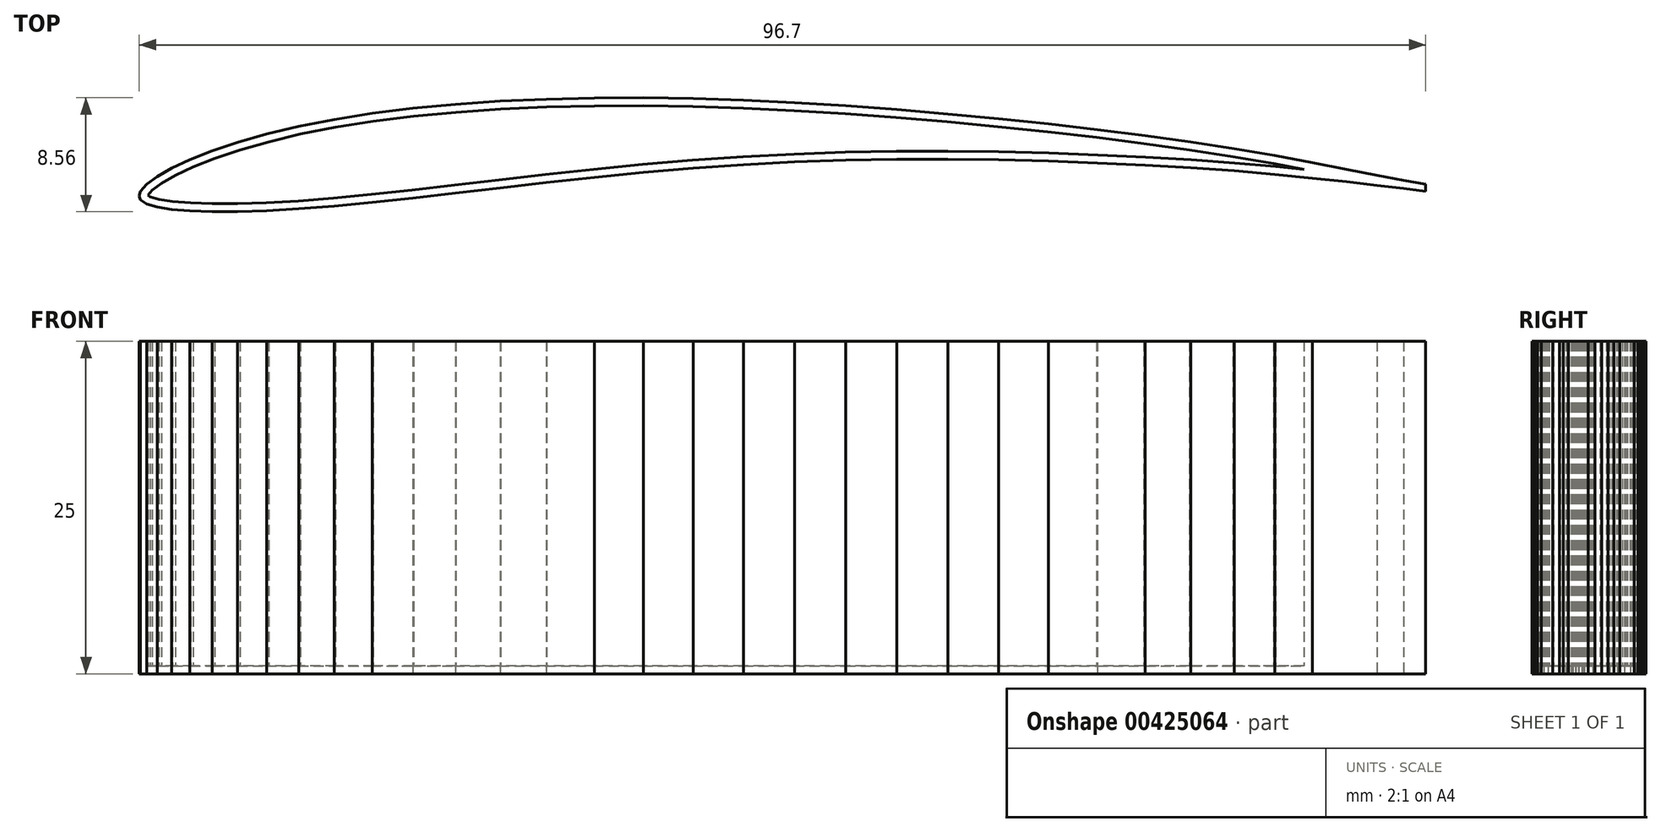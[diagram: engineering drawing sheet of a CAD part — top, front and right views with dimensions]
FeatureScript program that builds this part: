
annotation { "Feature Type Name" : "Feature", "Feature Type Description" : "" }
export const myFeature = defineFeature(function(context is Context, id is Id, definition is map)
    precondition{}
    {
        {
            var Q0;
            Q0=qCreatedBy(makeId("Top.planeOp"),FACE);
            var sketch = newSketch(context, id + "F0", { "sketchPlane" : qUnion([Q0])});
            skLineSegment(sketch, "E0", {"start": v(46.7, -2.2) * mm, "end": v(45.04, -1.92) * mm});
            skLineSegment(sketch, "E1", {"start": v(45.04, -1.92) * mm, "end": v(43.06, -1.56) * mm});
            skLineSegment(sketch, "E2", {"start": v(43.06, -1.56) * mm, "end": v(40.78, -1.1) * mm});
            skLineSegment(sketch, "E3", {"start": v(40.78, -1.1) * mm, "end": v(38.2, -0.6) * mm});
            skLineSegment(sketch, "E4", {"start": v(38.2, -0.6) * mm, "end": v(35.37, -0.07) * mm});
            skLineSegment(sketch, "E5", {"start": v(35.37, -0.07) * mm, "end": v(32.3, 0.45) * mm});
            skLineSegment(sketch, "E6", {"start": v(32.3, 0.45) * mm, "end": v(29.05, 0.96) * mm});
            skLineSegment(sketch, "E7", {"start": v(29.05, 0.96) * mm, "end": v(25.62, 1.44) * mm});
            skLineSegment(sketch, "E8", {"start": v(25.62, 1.44) * mm, "end": v(22.04, 1.9) * mm});
            skLineSegment(sketch, "E9", {"start": v(22.04, 1.9) * mm, "end": v(18.36, 2.31) * mm});
            skLineSegment(sketch, "E10", {"start": v(18.36, 2.31) * mm, "end": v(14.6, 2.7) * mm});
            skLineSegment(sketch, "E11", {"start": v(14.6, 2.7) * mm, "end": v(10.78, 3.07) * mm});
            skLineSegment(sketch, "E12", {"start": v(10.78, 3.07) * mm, "end": v(6.94, 3.4) * mm});
            skLineSegment(sketch, "E13", {"start": v(6.94, 3.4) * mm, "end": v(3.1, 3.68) * mm});
            skLineSegment(sketch, "E14", {"start": v(3.1, 3.68) * mm, "end": v(-0.73, 3.92) * mm});
            skLineSegment(sketch, "E15", {"start": v(-0.73, 3.92) * mm, "end": v(-4.56, 4.1) * mm});
            skLineSegment(sketch, "E16", {"start": v(-4.56, 4.1) * mm, "end": v(-8.36, 4.22) * mm});
            skLineSegment(sketch, "E17", {"start": v(-8.36, 4.22) * mm, "end": v(-12.11, 4.28) * mm});
            skLineSegment(sketch, "E18", {"start": v(-12.11, 4.28) * mm, "end": v(-15.8, 4.27) * mm});
            skLineSegment(sketch, "E19", {"start": v(-15.8, 4.27) * mm, "end": v(-19.4, 4.18) * mm});
            skLineSegment(sketch, "E20", {"start": v(-19.4, 4.18) * mm, "end": v(-22.88, 4.03) * mm});
            skLineSegment(sketch, "E21", {"start": v(-22.88, 4.03) * mm, "end": v(-26.24, 3.8) * mm});
            skLineSegment(sketch, "E22", {"start": v(-26.24, 3.8) * mm, "end": v(-29.45, 3.5) * mm});
            skLineSegment(sketch, "E23", {"start": v(-29.45, 3.5) * mm, "end": v(-32.5, 3.11) * mm});
            skLineSegment(sketch, "E24", {"start": v(-32.5, 3.11) * mm, "end": v(-35.35, 2.66) * mm});
            skLineSegment(sketch, "E25", {"start": v(-35.35, 2.66) * mm, "end": v(-38, 2.14) * mm});
            skLineSegment(sketch, "E26", {"start": v(-38, 2.14) * mm, "end": v(-40.42, 1.56) * mm});
            skLineSegment(sketch, "E27", {"start": v(-40.42, 1.56) * mm, "end": v(-42.6, 0.93) * mm});
            skLineSegment(sketch, "E28", {"start": v(-42.6, 0.93) * mm, "end": v(-44.53, 0.28) * mm});
            skLineSegment(sketch, "E29", {"start": v(-44.53, 0.28) * mm, "end": v(-46.19, -0.37) * mm});
            skLineSegment(sketch, "E30", {"start": v(-46.19, -0.37) * mm, "end": v(-47.57, -1.02) * mm});
            skLineSegment(sketch, "E31", {"start": v(-47.57, -1.02) * mm, "end": v(-48.66, -1.64) * mm});
            skLineSegment(sketch, "E32", {"start": v(-48.66, -1.64) * mm, "end": v(-49.45, -2.22) * mm});
            skLineSegment(sketch, "E33", {"start": v(-49.45, -2.22) * mm, "end": v(-49.9, -2.75) * mm});
            skLineSegment(sketch, "E34", {"start": v(-49.9, -2.75) * mm, "end": v(-50, -3.1) * mm});
            skLineSegment(sketch, "E35", {"start": v(-50, -3.1) * mm, "end": v(-49.9, -3.38) * mm});
            skLineSegment(sketch, "E36", {"start": v(-49.9, -3.38) * mm, "end": v(-49.45, -3.7) * mm});
            skLineSegment(sketch, "E37", {"start": v(-49.45, -3.7) * mm, "end": v(-48.66, -3.94) * mm});
            skLineSegment(sketch, "E38", {"start": v(-48.66, -3.94) * mm, "end": v(-47.57, -4.1) * mm});
            skLineSegment(sketch, "E39", {"start": v(-47.57, -4.1) * mm, "end": v(-46.19, -4.22) * mm});
            skLineSegment(sketch, "E40", {"start": v(-46.19, -4.22) * mm, "end": v(-44.53, -4.28) * mm});
            skLineSegment(sketch, "E41", {"start": v(-44.53, -4.28) * mm, "end": v(-42.6, -4.28) * mm});
            skLineSegment(sketch, "E42", {"start": v(-42.6, -4.28) * mm, "end": v(-40.42, -4.2) * mm});
            skLineSegment(sketch, "E43", {"start": v(-40.42, -4.2) * mm, "end": v(-38, -4.07) * mm});
            skLineSegment(sketch, "E44", {"start": v(-38, -4.07) * mm, "end": v(-35.35, -3.86) * mm});
            skLineSegment(sketch, "E45", {"start": v(-35.35, -3.86) * mm, "end": v(-32.5, -3.58) * mm});
            skLineSegment(sketch, "E46", {"start": v(-32.5, -3.58) * mm, "end": v(-29.45, -3.25) * mm});
            skLineSegment(sketch, "E47", {"start": v(-29.45, -3.25) * mm, "end": v(-26.24, -2.88) * mm});
            skLineSegment(sketch, "E48", {"start": v(-26.24, -2.88) * mm, "end": v(-22.88, -2.49) * mm});
            skLineSegment(sketch, "E49", {"start": v(-22.88, -2.49) * mm, "end": v(-19.4, -2.08) * mm});
            skLineSegment(sketch, "E50", {"start": v(-19.4, -2.08) * mm, "end": v(-15.8, -1.7) * mm});
            skLineSegment(sketch, "E51", {"start": v(-15.8, -1.7) * mm, "end": v(-12.11, -1.33) * mm});
            skLineSegment(sketch, "E52", {"start": v(-12.11, -1.33) * mm, "end": v(-8.36, -1.01) * mm});
            skLineSegment(sketch, "E53", {"start": v(-8.36, -1.01) * mm, "end": v(-4.56, -0.75) * mm});
            skLineSegment(sketch, "E54", {"start": v(-4.56, -0.75) * mm, "end": v(-0.74, -0.55) * mm});
            skLineSegment(sketch, "E55", {"start": v(-0.73, -0.55) * mm, "end": v(3.1, -0.41) * mm});
            skLineSegment(sketch, "E56", {"start": v(3.1, -0.41) * mm, "end": v(6.94, -0.34) * mm});
            skLineSegment(sketch, "E57", {"start": v(6.94, -0.34) * mm, "end": v(10.78, -0.33) * mm});
            skLineSegment(sketch, "E58", {"start": v(10.78, -0.33) * mm, "end": v(14.6, -0.38) * mm});
            skLineSegment(sketch, "E59", {"start": v(14.6, -0.38) * mm, "end": v(18.36, -0.48) * mm});
            skLineSegment(sketch, "E60", {"start": v(18.36, -0.48) * mm, "end": v(22.04, -0.62) * mm});
            skLineSegment(sketch, "E61", {"start": v(22.04, -0.62) * mm, "end": v(25.62, -0.78) * mm});
            skLineSegment(sketch, "E62", {"start": v(25.62, -0.78) * mm, "end": v(29.05, -0.98) * mm});
            skLineSegment(sketch, "E63", {"start": v(29.05, -0.98) * mm, "end": v(32.3, -1.21) * mm});
            skLineSegment(sketch, "E64", {"start": v(32.3, -1.21) * mm, "end": v(35.37, -1.47) * mm});
            skLineSegment(sketch, "E65", {"start": v(35.37, -1.47) * mm, "end": v(38.2, -1.75) * mm});
            skLineSegment(sketch, "E66", {"start": v(38.2, -1.75) * mm, "end": v(40.78, -2.04) * mm});
            skLineSegment(sketch, "E67", {"start": v(40.78, -2.04) * mm, "end": v(43.06, -2.3) * mm});
            skLineSegment(sketch, "E68", {"start": v(43.06, -2.3) * mm, "end": v(45.04, -2.54) * mm});
            skLineSegment(sketch, "E69", {"start": v(45.04, -2.54) * mm, "end": v(46.7, -2.74) * mm});
            skLineSegment(sketch, "E70", {"start": v(-50, -3.07) * mm, "end": v(50, -3.07) * mm, "construction": true});
            skLineSegment(sketch, "E71", {"start": v(46.7, -2.2) * mm, "end": v(46.7, -2.74) * mm});
            skLineSegment(sketch, "E72", {"start": v(35.37, -0.07) * mm, "end": v(35.37, -1.47) * mm});
            skSolve(sketch);
        }
        {
            var Q0;
            Q0 = qSketchRegion(id + "F0", true);
            extrude(context, id + "F1", {"entities" : qUnion([Q0]), "depth" : 25 * mm});
        }
        {
            var Q0;
            Q0=makeQuery(id+"F1.opExtrude","CAP_FACE",FACE,{"disambiguationData":[OSD([sQuery(id+"F0.wireOp",EDGE,"727b936a-63c7-4c52-894b-6a5cdd6f010b"),sQuery(id+"F0.wireOp",EDGE,"iox4s91j-Nup9-9dsc-COxM-rL3S8vBAQRYW")])],"isStart":false});
            var Q1;
            Q1=makeQuery(id+"F1.opExtrude","CAP_FACE",FACE,{"disambiguationData":[OSD([sQuery(id+"F0.wireOp",EDGE,"E0"),sQuery(id+"F0.wireOp",EDGE,"E1"),sQuery(id+"F0.wireOp",EDGE,"E2"),sQuery(id+"F0.wireOp",EDGE,"E3"),sQuery(id+"F0.wireOp",EDGE,"E4"),sQuery(id+"F0.wireOp",EDGE,"E5"),sQuery(id+"F0.wireOp",EDGE,"E6"),sQuery(id+"F0.wireOp",EDGE,"E7"),sQuery(id+"F0.wireOp",EDGE,"E8"),sQuery(id+"F0.wireOp",EDGE,"E9"),sQuery(id+"F0.wireOp",EDGE,"E10"),sQuery(id+"F0.wireOp",EDGE,"E11"),sQuery(id+"F0.wireOp",EDGE,"E12"),sQuery(id+"F0.wireOp",EDGE,"E13"),sQuery(id+"F0.wireOp",EDGE,"E14"),sQuery(id+"F0.wireOp",EDGE,"E15"),sQuery(id+"F0.wireOp",EDGE,"E16"),sQuery(id+"F0.wireOp",EDGE,"E17"),sQuery(id+"F0.wireOp",EDGE,"E18"),sQuery(id+"F0.wireOp",EDGE,"E19"),sQuery(id+"F0.wireOp",EDGE,"E20"),sQuery(id+"F0.wireOp",EDGE,"E21"),sQuery(id+"F0.wireOp",EDGE,"E22"),sQuery(id+"F0.wireOp",EDGE,"E23"),sQuery(id+"F0.wireOp",EDGE,"E24"),sQuery(id+"F0.wireOp",EDGE,"E25"),sQuery(id+"F0.wireOp",EDGE,"E26"),sQuery(id+"F0.wireOp",EDGE,"E27"),sQuery(id+"F0.wireOp",EDGE,"E28"),sQuery(id+"F0.wireOp",EDGE,"E29"),sQuery(id+"F0.wireOp",EDGE,"E30"),sQuery(id+"F0.wireOp",EDGE,"E31"),sQuery(id+"F0.wireOp",EDGE,"E32"),sQuery(id+"F0.wireOp",EDGE,"E33"),sQuery(id+"F0.wireOp",EDGE,"E34"),sQuery(id+"F0.wireOp",EDGE,"E35"),sQuery(id+"F0.wireOp",EDGE,"E36"),sQuery(id+"F0.wireOp",EDGE,"E37"),sQuery(id+"F0.wireOp",EDGE,"E38"),sQuery(id+"F0.wireOp",EDGE,"E39"),sQuery(id+"F0.wireOp",EDGE,"E40"),sQuery(id+"F0.wireOp",EDGE,"E41"),sQuery(id+"F0.wireOp",EDGE,"E42"),sQuery(id+"F0.wireOp",EDGE,"E43"),sQuery(id+"F0.wireOp",EDGE,"E44"),sQuery(id+"F0.wireOp",EDGE,"E45"),sQuery(id+"F0.wireOp",EDGE,"E46"),sQuery(id+"F0.wireOp",EDGE,"E47"),sQuery(id+"F0.wireOp",EDGE,"E48"),sQuery(id+"F0.wireOp",EDGE,"E49"),sQuery(id+"F0.wireOp",EDGE,"E50"),sQuery(id+"F0.wireOp",EDGE,"E51"),sQuery(id+"F0.wireOp",EDGE,"E52"),sQuery(id+"F0.wireOp",EDGE,"E53"),sQuery(id+"F0.wireOp",EDGE,"E54"),sQuery(id+"F0.wireOp",EDGE,"E55"),sQuery(id+"F0.wireOp",EDGE,"E56"),sQuery(id+"F0.wireOp",EDGE,"E57"),sQuery(id+"F0.wireOp",EDGE,"E58"),sQuery(id+"F0.wireOp",EDGE,"E59"),sQuery(id+"F0.wireOp",EDGE,"E60"),sQuery(id+"F0.wireOp",EDGE,"E61"),sQuery(id+"F0.wireOp",EDGE,"E62"),sQuery(id+"F0.wireOp",EDGE,"E63"),sQuery(id+"F0.wireOp",EDGE,"E64"),sQuery(id+"F0.wireOp",EDGE,"E65"),sQuery(id+"F0.wireOp",EDGE,"E66"),sQuery(id+"F0.wireOp",EDGE,"E67"),sQuery(id+"F0.wireOp",EDGE,"E68"),sQuery(id+"F0.wireOp",EDGE,"E69"),sQuery(id+"F0.wireOp",EDGE,"E71")])],"isStart":false});
            shell(context, id + "F2", {"entities" : qUnion([Q0, Q1]), "thickness" : 0.6 * mm});
        }
        {
            var Q0;
            Q0=qCreatedBy(makeId("Front.planeOp"),FACE);
            cPlane(context, id + "F3", {"entities" : qUnion([Q0]), "cplaneType" : CPlaneType.OFFSET, "offset" : 10 * mm, "width" : 150 * mm, "height" : 150 * mm});
        }
    });
